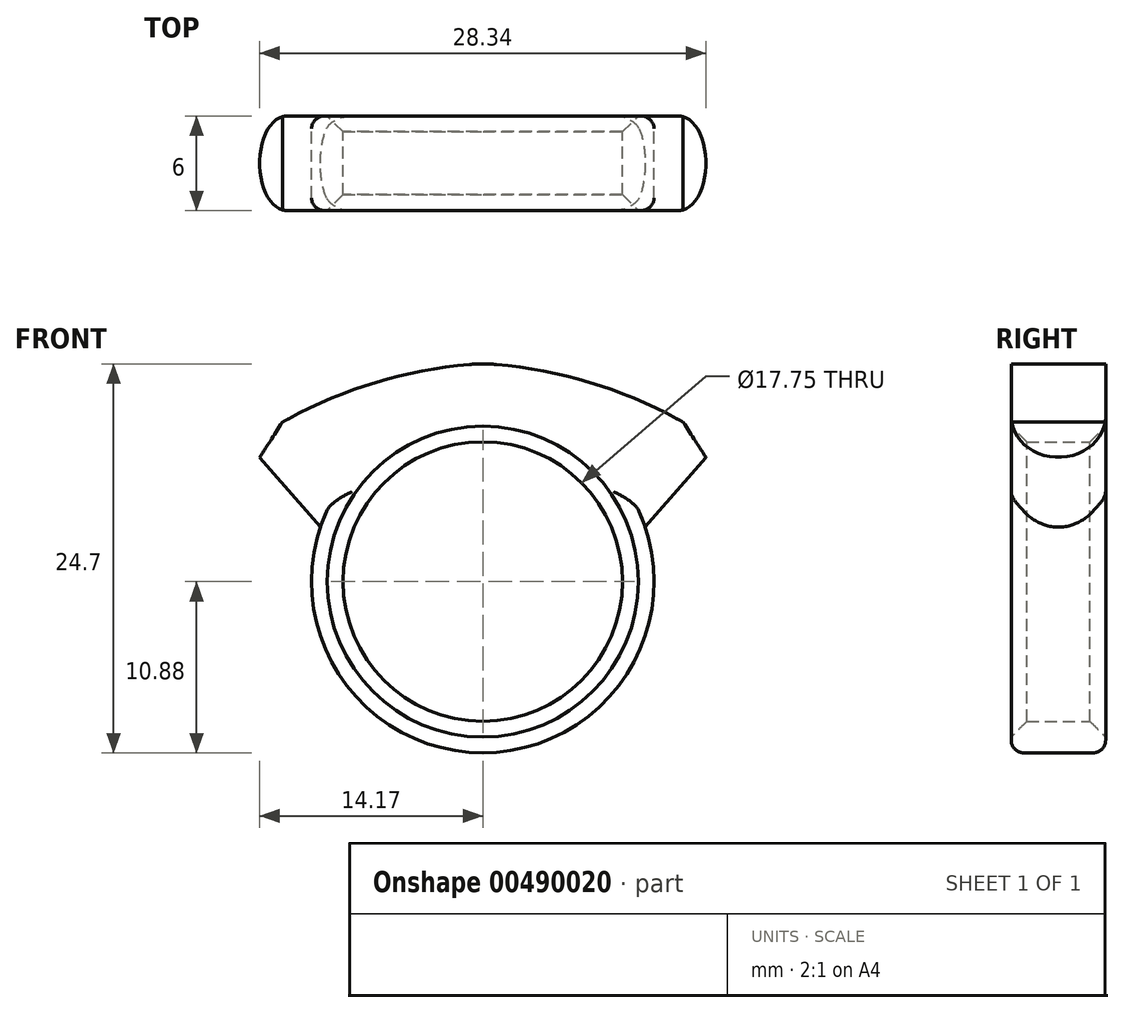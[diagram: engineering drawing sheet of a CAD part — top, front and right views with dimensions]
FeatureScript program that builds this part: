
annotation { "Feature Type Name" : "Feature", "Feature Type Description" : "" }
export const myFeature = defineFeature(function(context is Context, id is Id, definition is map)
    precondition{}
    {
        {
            var Q0;
            Q0=qCreatedBy(makeId("Front.planeOp"),FACE);
            var sketch = newSketch(context, id + "F0", { "sketchPlane" : qUnion([Q0])});
            skCircle(sketch, "E0", {"center": v(0, 0) * mm, "radius": 8.88 * mm});
            skCircle(sketch, "E1.0", {"center": v(0, 0) * mm, "radius": 10.88 * mm});
            skLineSegment(sketch, "E2", {"start": v(-10.31, 3.46) * mm, "end": v(-14.17, 7.88) * mm});
            skLineSegment(sketch, "E3", {"start": v(-14.17, 7.88) * mm, "end": v(-12.73, 10.12) * mm});
            skLineSegment(sketch, "E4", {"start": v(-12.73, 10.12) * mm, "end": v(-10.31, 3.46) * mm});
            skArc(sketch, "E5", {"start": v(0, 13.85) * mm, "mid": v(-6.58, 12.72) * mm, "end": v(-12.73, 10.12) * mm});
            skArc(sketch, "E6.MirrorCS", {"start": v(0, 13.85) * mm, "mid": v(6.58, 12.72) * mm, "end": v(12.73, 10.12) * mm});
            skLineSegment(sketch, "E7.MirrorCS", {"start": v(14.17, 7.88) * mm, "end": v(12.73, 10.12) * mm});
            skLineSegment(sketch, "E8.MirrorCS", {"start": v(10.31, 3.46) * mm, "end": v(14.17, 7.88) * mm});
            skSolve(sketch);
        }
        {
            var Q0;
            {var subQ0=sQuery(id+"F0.wireOp",EDGE,"E4");Q0=makeQuery(id+"F0.imprint","IMPRINT",FACE,{"disambiguationData":[TD([[makeQuery(id+"F0.imprint","IMPRINT",EDGE,{"derivedFrom":subQ0}),1.0]])]});}
            var Q1;
            Q1=makeQuery(id+"F0.imprint","IMPRINT",FACE,{"disambiguationData":[TD([[makeQuery(id+"F0.imprint","IMPRINT",EDGE,{"derivedFrom":sQuery(id+"F0.wireOp",EDGE,"E2")}),-1.0]])]});
            var Q2;
            Q2=makeQuery(id+"F0.imprint","IMPRINT",FACE,{"disambiguationData":[TD([[makeQuery(id+"F0.imprint","IMPRINT",EDGE,{"derivedFrom":sQuery(id+"F0.wireOp",EDGE,"E0")}),-1.0]])]});
            extrude(context, id + "F1", {"entities" : qUnion([Q0, Q1, Q2]), "depth" : 3 * mm, "offsetDistance" : 25 * mm, "hasSecondDirection" : true, "secondDirectionOppositeDirection" : true, "secondDirectionDepth" : 3 * mm});
        }
        {
            var Q0;
            Q0=makeQuery(id+"F1.opExtrude","CAP_EDGE",EDGE,{"disambiguationData":[OSD([sQuery(id+"F0.wireOp",EDGE,"E8.MirrorCS")])],"isStart":false});
            var Q1;
            Q1=makeQuery(id+"F1.opExtrude","CAP_EDGE",EDGE,{"disambiguationData":[OSD([sQuery(id+"F0.wireOp",EDGE,"E8.MirrorCS")])],"isStart":true});
            var Q2;
            Q2=makeQuery(id+"F1.opExtrude","CAP_EDGE",EDGE,{"disambiguationData":[OSD([sQuery(id+"F0.wireOp",EDGE,"E2")])],"isStart":false});
            var Q3;
            Q3=makeQuery(id+"F1.opExtrude","CAP_EDGE",EDGE,{"disambiguationData":[OSD([sQuery(id+"F0.wireOp",EDGE,"E2")])],"isStart":true});
            fillet(context, id + "F2", {"entities" : qUnion([Q0, Q1, Q2, Q3]), "radius" : 3 * mm, "tangentPropagation" : true, "allowEdgeOverflow" : false});
        }
        {
            var Q0;
            Q0=makeQuery(id+"F1.opExtrude","CAP_EDGE",EDGE,{"disambiguationData":[OSD([sQuery(id+"F0.wireOp",EDGE,"E0")])],"isStart":false});
            var Q1;
            Q1=makeQuery(id+"F1.opExtrude","CAP_EDGE",EDGE,{"disambiguationData":[OSD([sQuery(id+"F0.wireOp",EDGE,"E0")])],"isStart":true});
            chamfer(context, id + "F3", {"entities" : qUnion([Q0, Q1]), "width" : 1 * mm, "tangentPropagation" : true});
        }
        {
            var Q0;
            Q0=makeQuery(id+"F1.opExtrude","CAP_EDGE",EDGE,{"disambiguationData":[OSD([sQuery(id+"F0.wireOp",EDGE,"E1.0")])],"isStart":true});
            var Q1;
            Q1=makeQuery(id+"F1.opExtrude","CAP_EDGE",EDGE,{"disambiguationData":[OSD([sQuery(id+"F0.wireOp",EDGE,"E1.0")])],"isStart":false});
            fillet(context, id + "F4", {"entities" : qUnion([Q0, Q1]), "radius" : .8 * mm, "tangentPropagation" : true, "allowEdgeOverflow" : false});
        }
        {
            var Q0;
            Q0=makeQuery(id+"F1.opExtrude","SWEPT_EDGE",EDGE,{"disambiguationData":[OSD([sQuery(id+"F0.wireOp",EDGE,"E5"),sQuery(id+"F0.wireOp",EDGE,"E6.MirrorCS")])]});
            fillet(context, id + "F5", {"entities" : qUnion([Q0]), "radius" : 10 * mm, "tangentPropagation" : true, "allowEdgeOverflow" : false});
        }
    });
